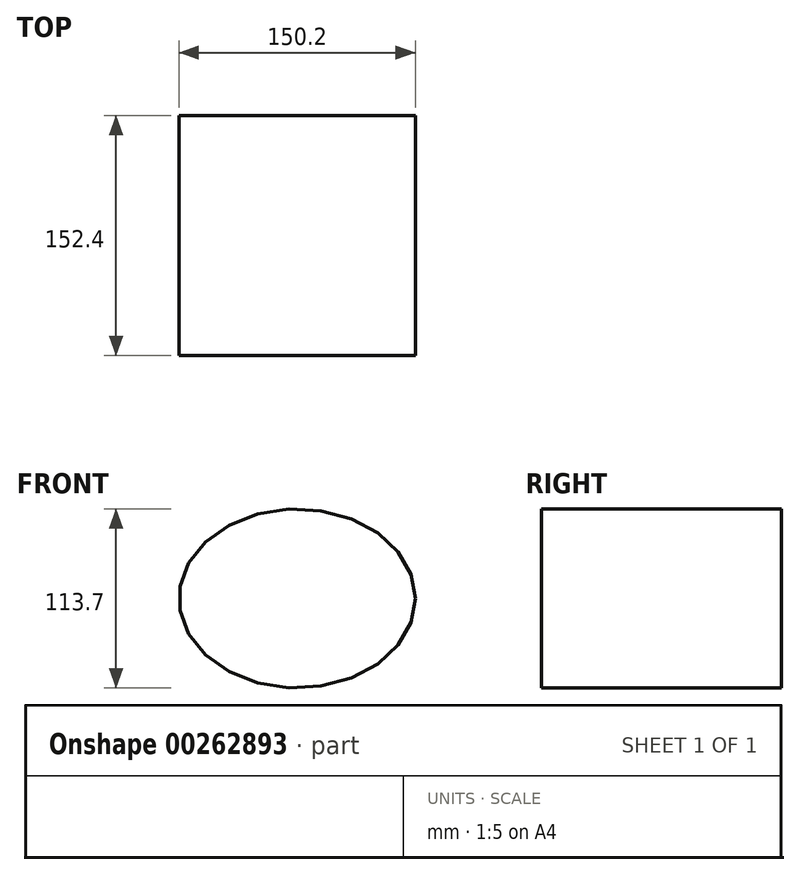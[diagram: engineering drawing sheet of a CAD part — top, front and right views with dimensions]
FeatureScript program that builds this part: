
annotation { "Feature Type Name" : "Feature", "Feature Type Description" : "" }
export const myFeature = defineFeature(function(context is Context, id is Id, definition is map)
    precondition{}
    {
        {
            var Q0;
            Q0=qCreatedBy(makeId("Front.planeOp"),FACE);
            var sketch = newSketch(context, id + "F0", { "sketchPlane" : qUnion([Q0])});
            skEllipse(sketch, "E0", {"center": v(0, 0) * mm, "majorRadius": 75.1 * mm, "minorRadius": 56.85 * mm, "majorAxis": v(1, 0)});
            skSolve(sketch);
        }
        {
            var Q0;
            Q0=sQuery(id+"F0.wireOp",EDGE,"E0");
            extrude(context, id + "F1", {"bodyType" : ToolBodyType.SURFACE, "surfaceEntities" : qUnion([Q0]), "depth" : 152.4 * mm});
        }
    });
